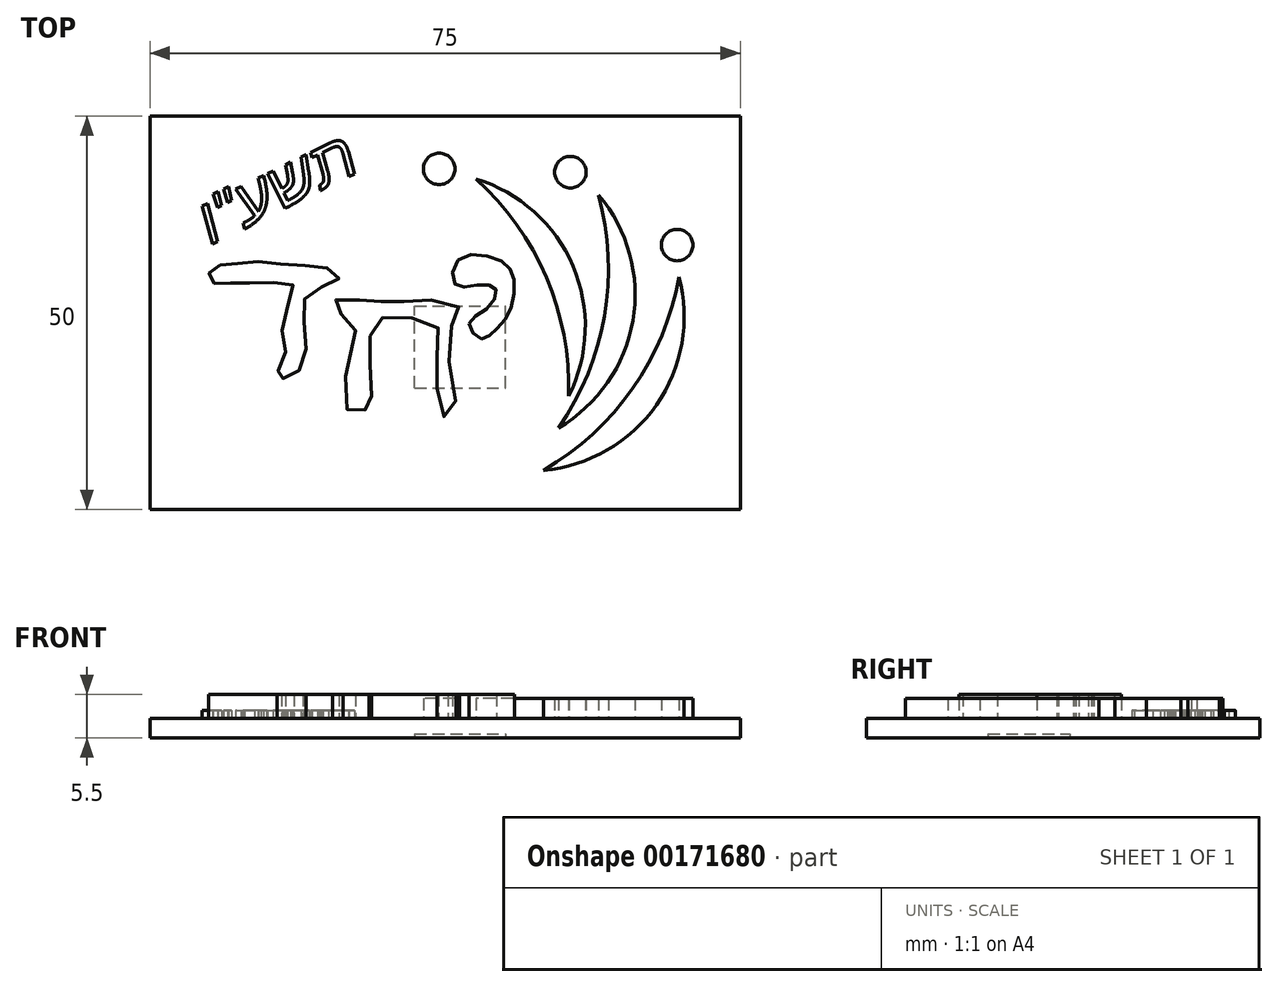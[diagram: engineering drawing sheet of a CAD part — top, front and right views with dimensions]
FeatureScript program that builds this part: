
annotation { "Feature Type Name" : "Feature", "Feature Type Description" : "" }
export const myFeature = defineFeature(function(context is Context, id is Id, definition is map)
    precondition{}
    {
        {
            var Q0;
            Q0=qCreatedBy(makeId("Top.planeOp"),FACE);
            var sketch = newSketch(context, id + "F0", { "sketchPlane" : qUnion([Q0])});
            skLineSegment(sketch, "E0.bottom", {"start": v(-37.5, 25) * mm, "end": v(37.5, 25) * mm});
            skLineSegment(sketch, "E0.top", {"start": v(-37.5, -25) * mm, "end": v(37.5, -25) * mm});
            skLineSegment(sketch, "E0.left", {"start": v(-37.5, 25) * mm, "end": v(-37.5, -25) * mm});
            skLineSegment(sketch, "E0.right", {"start": v(37.5, 25) * mm, "end": v(37.5, -25) * mm});
            skPoint(sketch, "E0.middle", {"position": v(0, 0) * mm});
            skSolve(sketch);
        }
        {
            var Q0;
            Q0 = qSketchRegion(id + "F0", true);
            extrude(context, id + "F1", {"entities" : qUnion([Q0]), "depth" : 2.5 * mm});
        }
        {
            var Q0;
            Q0=makeQuery(id+"F1.opExtrude","CAP_FACE",FACE,{"disambiguationData":[OSD([sQuery(id+"F0.wireOp",EDGE,"E0.bottom"),sQuery(id+"F0.wireOp",EDGE,"E0.top"),sQuery(id+"F0.wireOp",EDGE,"E0.left"),sQuery(id+"F0.wireOp",EDGE,"E0.right")])],"isStart":false});
            var sketch = newSketch(context, id + "F2", { "sketchPlane" : qUnion([Q0])});
            skArc(sketch, "E1", {"start": v(12.5, -20) * mm, "mid": v(23.83, -9.62) * mm, "end": v(29.7, 4.57) * mm});
            skArc(sketch, "E2", {"start": v(12.5, -20) * mm, "mid": v(26.83, -11.72) * mm, "end": v(29.7, 4.57) * mm});
            skLineSegment(sketch, "E3", {"start": v(29.7, 4.57) * mm, "end": v(12.5, -20) * mm, "construction": true});
            skLineSegment(sketch, "E4", {"start": v(12.5, -20) * mm, "end": v(10.8, -0.5) * mm, "construction": true});
            skLineSegment(sketch, "E5", {"start": v(10.8, -0.5) * mm, "end": v(29.7, 4.57) * mm, "construction": true});
            skLineSegment(sketch, "E6", {"start": v(12.5, -20) * mm, "end": v(-5.25, 10.74) * mm, "construction": true});
            skLineSegment(sketch, "E7", {"start": v(29.7, 4.57) * mm, "end": v(-5.25, 10.74) * mm, "construction": true});
            skArc(sketch, "E8", {"start": v(14.42, -14.6) * mm, "mid": v(20.24, -0.39) * mm, "end": v(19.5, 14.96) * mm});
            skArc(sketch, "E9", {"start": v(14.42, -14.6) * mm, "mid": v(23.86, -1) * mm, "end": v(19.5, 14.96) * mm});
            skLineSegment(sketch, "E10", {"start": v(19.5, 14.96) * mm, "end": v(14.42, -14.6) * mm, "construction": true});
            skArc(sketch, "E11", {"start": v(15.7, -10.6) * mm, "mid": v(12.87, 4.5) * mm, "end": v(3.92, 17) * mm});
            skArc(sketch, "E12", {"start": v(15.7, -10.6) * mm, "mid": v(16.24, 5.95) * mm, "end": v(3.92, 17) * mm});
            skLineSegment(sketch, "E13", {"start": v(3.92, 17) * mm, "end": v(15.7, -10.6) * mm, "construction": true});
            skCircle(sketch, "E14", {"center": v(29.48, 8.6) * mm, "radius": 2 * mm});
            skCircle(sketch, "E15", {"center": v(15.91, 17.87) * mm, "radius": 2 * mm});
            skCircle(sketch, "E16", {"center": v(-0.75, 18.28) * mm, "radius": 2 * mm});
            skSolve(sketch);
        }
        {
            var Q0;
            Q0 = qSketchRegion(id + "F2", true);
            extrude(context, id + "F3", {"entities" : qUnion([Q0]), "operationType" : NewBodyOperationType.ADD, "depth" : 2.5 * mm});
        }
        {
            var Q0;
            Q0=makeQuery(id+"F1.opExtrude","CAP_FACE",FACE,{"disambiguationData":[OSD([sQuery(id+"F0.wireOp",EDGE,"E0.bottom"),sQuery(id+"F0.wireOp",EDGE,"E0.top"),sQuery(id+"F0.wireOp",EDGE,"E0.left"),sQuery(id+"F0.wireOp",EDGE,"E0.right")])],"isStart":false});
            var sketch = newSketch(context, id + "F4", { "sketchPlane" : qUnion([Q0])});
            skFitSpline(sketch, "E17", {"points": [v(3.03, -1.34) * mm, v(4.53, -3.3) * mm, v(6.03, -2.51) * mm, v(8.12, 0) * mm, v(8.7, 4.47) * mm, v(6.75, 6.75) * mm, v(1.73, 6.75) * mm, v(1.34, 3.55) * mm, v(4.4, 3.55) * mm, v(6.42, 3.03) * mm, v(5.38, 0.55) * mm, v(3.03, -1.34) * mm]});
            skFitSpline(sketch, "E18", {"points": [v(-8.12, 1.4) * mm, v(-5.64, 1.47) * mm, v(-3.75, 1.47) * mm, v(1.08, 1.34) * mm, v(1.8, 0) * mm, v(0.62, -2.12) * mm, v(0.95, -8.7) * mm, v(1.01, -12.88) * mm, v(-0.55, -12.95) * mm, v(-0.95, -7.99) * mm, v(-1.01, -4.73) * mm, v(-1.27, -1.14) * mm, v(-6.1, -0.75) * mm, v(-8.38, -0.75) * mm, v(-9.55, -3.16) * mm, v(-9.49, -6.68) * mm, v(-9.36, -10.8) * mm, v(-9.49, -11.7) * mm, v(-10.6, -12.55) * mm, v(-12.23, -12.49) * mm, v(-12.82, -8.97) * mm, v(-11.51, -1.08) * mm, v(-13.53, 0) * mm, v(-14.28, 1.14) * mm, v(-12.63, 2.01) * mm, v(-10.14, 1.4) * mm, v(-8.12, 1.4) * mm]});
            skFitSpline(sketch, "E19", {"points": [v(-23.77, 6.49) * mm, v(-19.14, 6.03) * mm, v(-14.74, 5.62) * mm, v(-13.53, 4.2) * mm, v(-17.18, 2.64) * mm, v(-17.97, -0.88) * mm, v(-18.03, -6.55) * mm, v(-20.38, -8.32) * mm, v(-21.36, -7.99) * mm, v(-20.32, -5.38) * mm, v(-20.7, -1.14) * mm, v(-19.27, 3.49) * mm, v(-22.99, 3.75) * mm, v(-26.7, 3.82) * mm, v(-29.18, 3.68) * mm, v(-30.03, 4.57) * mm, v(-29.25, 5.84) * mm, v(-27.16, 6.16) * mm, v(-23.77, 6.49) * mm]});
            skSolve(sketch);
        }
        {
            var Q0;
            Q0 = qSketchRegion(id + "F4", true);
            extrude(context, id + "F5", {"entities" : qUnion([Q0]), "operationType" : NewBodyOperationType.ADD, "depth" : 3 * mm});
        }
        {
            var Q0;
            Q0=makeQuery(id+"F1.opExtrude","CAP_FACE",FACE,{"disambiguationData":[OSD([sQuery(id+"F0.wireOp",EDGE,"E0.bottom"),sQuery(id+"F0.wireOp",EDGE,"E0.top"),sQuery(id+"F0.wireOp",EDGE,"E0.left"),sQuery(id+"F0.wireOp",EDGE,"E0.right")])],"isStart":false});
            var sketch = newSketch(context, id + "F6", { "sketchPlane" : qUnion([Q0])});
            skText(sketch, "E20", { "text": "ו\"עשת", "fontName": "Arimo-Italic.ttf"});
            const initialGuessF6  = {"E20": [-0.0298, 0.00863, 0.89693, 0.44218, 0.0059]};
            skSetInitialGuess(sketch, initialGuessF6);
            skSolve(sketch);
        }
        {
            var Q0;
            Q0 = qSketchRegion(id + "F6", true);
            extrude(context, id + "F7", {"entities" : qUnion([Q0]), "operationType" : NewBodyOperationType.ADD, "depth" : 1 * mm});
        }
        {
            var Q0;
            Q0=makeQuery(id+"F1.opExtrude","CAP_FACE",FACE,{"disambiguationData":[OSD([sQuery(id+"F0.wireOp",EDGE,"E0.bottom"),sQuery(id+"F0.wireOp",EDGE,"E0.top"),sQuery(id+"F0.wireOp",EDGE,"E0.left"),sQuery(id+"F0.wireOp",EDGE,"E0.right")])],"isStart":true});
            var sketch = newSketch(context, id + "F8", { "sketchPlane" : qUnion([Q0])});
            skLineSegment(sketch, "E21.bottom", {"start": v(-19.35, 6.14) * mm, "end": v(-1.3, 6.14) * mm});
            skLineSegment(sketch, "E21.top", {"start": v(-19.35, -4.84) * mm, "end": v(-1.3, -4.84) * mm});
            skLineSegment(sketch, "E21.left", {"start": v(-19.35, 6.14) * mm, "end": v(-19.35, -4.84) * mm});
            skLineSegment(sketch, "E21.right", {"start": v(-1.3, 6.14) * mm, "end": v(-1.3, -4.84) * mm});
            skSolve(sketch);
        }
        {
            var Q0;
            Q0=makeQuery(id+"F8.imprint","IMPRINT",FACE,{"disambiguationData":[TD([[makeQuery(id+"F8.imprint","IMPRINT",EDGE,{"derivedFrom":sQuery(id+"F8.wireOp",EDGE,"E21.bottom")}),1.0]])]});
            var sketch = newSketch(context, id + "F9", { "sketchPlane" : qUnion([Q0])});
            skLineSegment(sketch, "E22.bottom", {"start": v(-3.88, 9.52) * mm, "end": v(7.7, 9.52) * mm});
            skLineSegment(sketch, "E22.top", {"start": v(-3.88, -0.88) * mm, "end": v(7.7, -0.88) * mm});
            skLineSegment(sketch, "E22.left", {"start": v(-3.88, 9.52) * mm, "end": v(-3.88, -0.88) * mm});
            skLineSegment(sketch, "E22.right", {"start": v(7.7, 9.52) * mm, "end": v(7.7, -0.88) * mm});
            skSolve(sketch);
        }
        {
            var Q0;
            Q0 = qSketchRegion(id + "F9", true);
            extrude(context, id + "F10", {"entities" : qUnion([Q0]), "operationType" : NewBodyOperationType.REMOVE, "oppositeDirection" : true, "depth" : .5 * mm});
        }
    });
